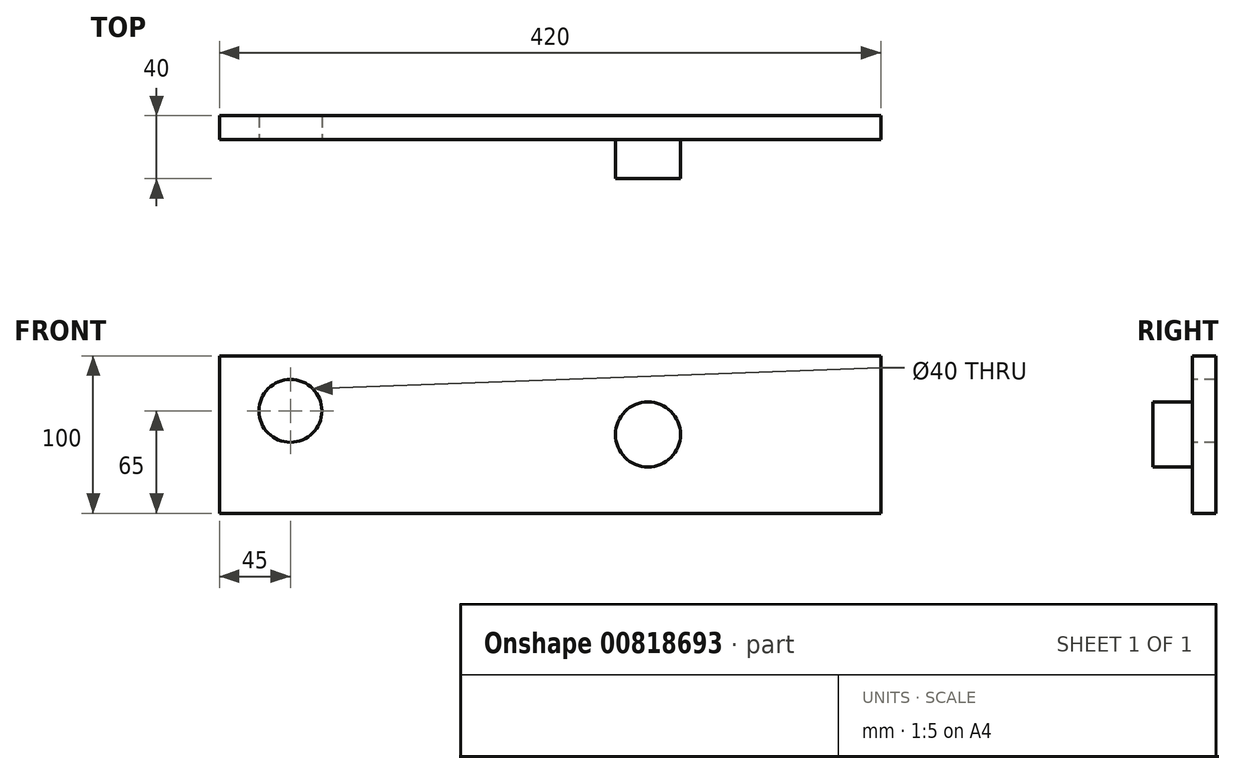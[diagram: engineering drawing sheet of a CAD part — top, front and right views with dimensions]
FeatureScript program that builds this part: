
annotation { "Feature Type Name" : "Feature", "Feature Type Description" : "" }
export const myFeature = defineFeature(function(context is Context, id is Id, definition is map)
    precondition{}
    {
        {
            var Q0;
            Q0=qCreatedBy(makeId("Front.planeOp"),FACE);
            var sketch = newSketch(context, id + "F0", { "sketchPlane" : qUnion([Q0])});
            skLineSegment(sketch, "E0.bottom", {"start": v(210, 50) * mm, "end": v(-210, 50) * mm});
            skLineSegment(sketch, "E0.top", {"start": v(210, -50) * mm, "end": v(-210, -50) * mm});
            skLineSegment(sketch, "E0.left", {"start": v(210, 50) * mm, "end": v(210, -50) * mm});
            skLineSegment(sketch, "E0.right", {"start": v(-210, 50) * mm, "end": v(-210, -50) * mm});
            skPoint(sketch, "E0.middle", {"position": v(0, 0) * mm});
            skSolve(sketch);
        }
        {
            var Q0;
            Q0 = qSketchRegion(id + "F0", true);
            extrude(context, id + "F1", {"entities" : qUnion([Q0]), "depth" : 15 * mm, "offsetDistance" : 25 * mm});
        }
        {
            var Q0;
            Q0=makeQuery(id+"F1.opExtrude","CAP_FACE",FACE,{"disambiguationData":[OSD([sQuery(id+"F0.wireOp",EDGE,"E0.bottom"),sQuery(id+"F0.wireOp",EDGE,"E0.top"),sQuery(id+"F0.wireOp",EDGE,"E0.left"),sQuery(id+"F0.wireOp",EDGE,"E0.right")])],"isStart":false});
            var sketch = newSketch(context, id + "F2", { "sketchPlane" : qUnion([Q0])});
            skCircle(sketch, "E1", {"center": v(-165, 15) * mm, "radius": 20 * mm});
            skSolve(sketch);
        }
        {
            var Q0;
            Q0 = qSketchRegion(id + "F2", true);
            extrude(context, id + "F3", {"entities" : qUnion([Q0]), "operationType" : NewBodyOperationType.REMOVE, "endBound" : BoundingType.THROUGH_ALL, "oppositeDirection" : true, "depth" : 25 * mm, "offsetDistance" : 25 * mm});
        }
        {
            var Q0;
            Q0=makeQuery(id+"F1.opExtrude","CAP_FACE",FACE,{"disambiguationData":[OSD([sQuery(id+"F0.wireOp",EDGE,"E0.bottom"),sQuery(id+"F0.wireOp",EDGE,"E0.top"),sQuery(id+"F0.wireOp",EDGE,"E0.left"),sQuery(id+"F0.wireOp",EDGE,"E0.right")])],"isStart":false});
            var sketch = newSketch(context, id + "F4", { "sketchPlane" : qUnion([Q0])});
            skCircle(sketch, "E2", {"center": v(62.06, 0) * mm, "radius": 20.67 * mm});
            skSolve(sketch);
        }
        {
            var Q0;
            Q0 = qSketchRegion(id + "F4", true);
            extrude(context, id + "F5", {"entities" : qUnion([Q0]), "operationType" : NewBodyOperationType.ADD, "depth" : 25 * mm, "offsetDistance" : 25 * mm});
        }
    });
